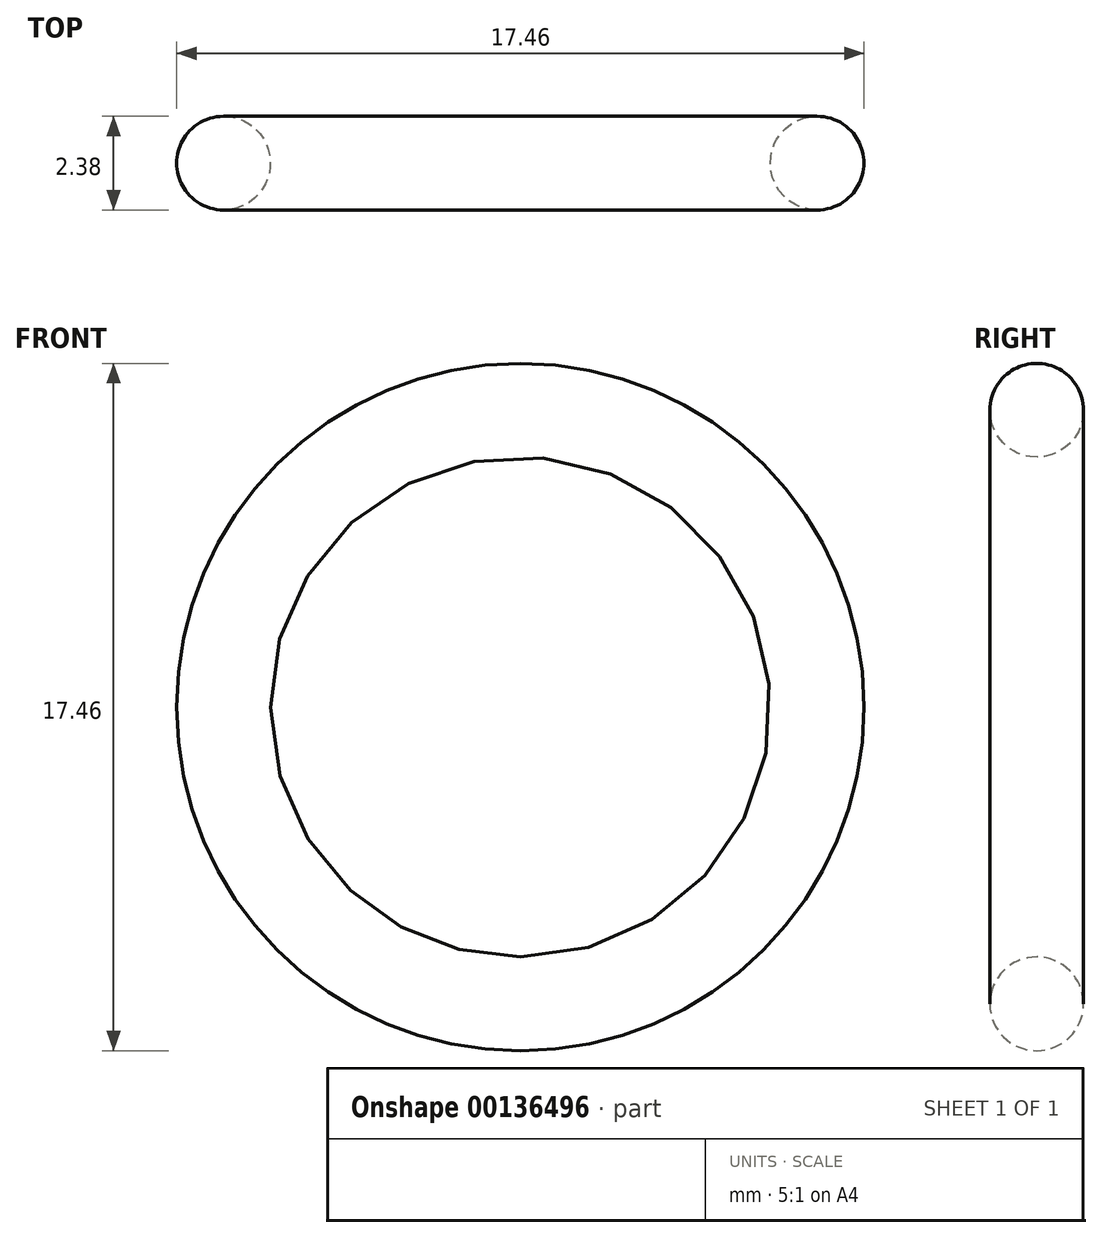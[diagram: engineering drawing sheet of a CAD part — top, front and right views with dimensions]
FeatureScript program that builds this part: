
annotation { "Feature Type Name" : "Feature", "Feature Type Description" : "" }
export const myFeature = defineFeature(function(context is Context, id is Id, definition is map)
    precondition{}
    {
        {
            var Q0;
            Q0=qCreatedBy(makeId("Right.planeOp"),FACE);
            var sketch = newSketch(context, id + "F0", { "sketchPlane" : qUnion([Q0])});
            skLineSegment(sketch, "E0", {"start": v(-25.93, 0) * mm, "end": v(26.74, 0) * mm});
            skCircle(sketch, "E1", {"center": v(0, 7.54) * mm, "radius": 1.2 * mm});
            skSolve(sketch);
        }
        {
            var Q0;
            Q0 = qSketchRegion(id + "F0", true);
            var Q1;
            Q1=sQuery(id+"F0.wireOp",EDGE,"E0");
            revolve(context, id + "F1", {"entities" : qUnion([Q0]), "axis" : qUnion([Q1]), "revolveType" : RevolveType.FULL});
        }
    });
